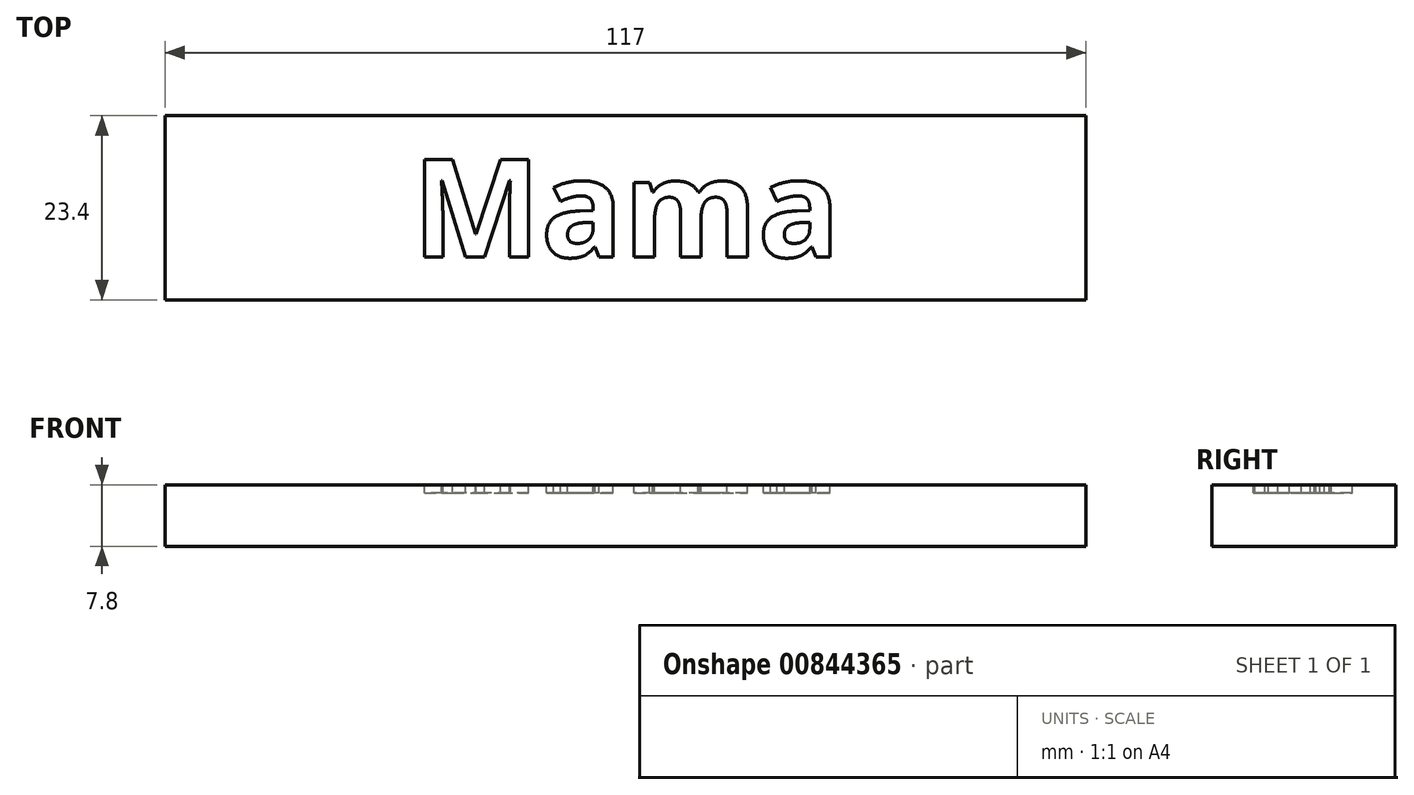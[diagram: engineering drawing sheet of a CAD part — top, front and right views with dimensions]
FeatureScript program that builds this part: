
annotation { "Feature Type Name" : "Feature", "Feature Type Description" : "" }
export const myFeature = defineFeature(function(context is Context, id is Id, definition is map)
    precondition{}
    {
        {
            var Q0;
            Q0=qCreatedBy(makeId("Top.planeOp"),FACE);
            var sketch = newSketch(context, id + "F0", { "sketchPlane" : qUnion([Q0])});
            skLineSegment(sketch, "E0.bottom", {"start": v(0, 0) * mm, "end": v(117, 0) * mm});
            skLineSegment(sketch, "E0.top", {"start": v(0, 23.4) * mm, "end": v(117, 23.4) * mm});
            skLineSegment(sketch, "E0.left", {"start": v(0, 0) * mm, "end": v(0, 23.4) * mm});
            skLineSegment(sketch, "E0.right", {"start": v(117, 0) * mm, "end": v(117, 23.4) * mm});
            skSolve(sketch);
        }
        {
            var Q0;
            Q0 = qSketchRegion(id + "F0", true);
            extrude(context, id + "F1", {"entities" : qUnion([Q0]), "depth" : 7.8 * mm, "offsetDistance" : 25 * mm});
        }
        {
            var Q0;
            Q0=makeQuery(id+"F1.opExtrude","CAP_FACE",FACE,{"disambiguationData":[OSD([sQuery(id+"F0.wireOp",EDGE,"E0.bottom"),sQuery(id+"F0.wireOp",EDGE,"E0.top"),sQuery(id+"F0.wireOp",EDGE,"E0.left"),sQuery(id+"F0.wireOp",EDGE,"E0.right")])],"isStart":false});
            var sketch = newSketch(context, id + "F2", { "sketchPlane" : qUnion([Q0])});
            skText(sketch, "E1", { "text": "Boaz", "fontName": "OpenSans-Bold.ttf"});
            skLineSegment(sketch, "E2", {"start": v(0, 11.7) * mm, "end": v(117, 11.7) * mm, "construction": true});
            skPoint(sketch, "E3", {"position": v(58.5, 11.7) * mm});
            const initialGuessF2  = {"E1": [0.03751, 0.00545, 1, 0, 0.0125]};
            skSetInitialGuess(sketch, initialGuessF2);
            skSolve(sketch);
        }
        {
            var Q0;
            Q0=makeQuery(id+"F1.opExtrude","CAP_FACE",FACE,{"disambiguationData":[OSD([sQuery(id+"F0.wireOp",EDGE,"E0.bottom"),sQuery(id+"F0.wireOp",EDGE,"E0.top"),sQuery(id+"F0.wireOp",EDGE,"E0.left"),sQuery(id+"F0.wireOp",EDGE,"E0.right")])],"isStart":false});
            var sketch = newSketch(context, id + "F3", { "sketchPlane" : qUnion([Q0])});
            skText(sketch, "E4", { "text": "Mama", "fontName": "OpenSans-Bold.ttf"});
            skLineSegment(sketch, "E5", {"start": v(0, 11.7) * mm, "end": v(117, 11.7) * mm, "construction": true});
            skPoint(sketch, "E6", {"position": v(58.5, 11.7) * mm});
            const initialGuessF3  = {"E4": [0.0314, 0.00545, 1, 0, 0.0125]};
            skSetInitialGuess(sketch, initialGuessF3);
            skSolve(sketch);
        }
        {
            var Q0;
            Q0 = qSketchRegion(id + "F3", true);
            extrude(context, id + "F4", {"entities" : qUnion([Q0]), "operationType" : NewBodyOperationType.REMOVE, "oppositeDirection" : true, "depth" : 1 * mm, "offsetDistance" : 25 * mm});
        }
    });
